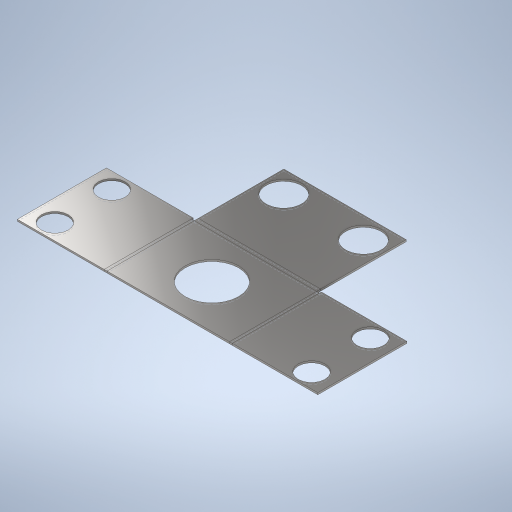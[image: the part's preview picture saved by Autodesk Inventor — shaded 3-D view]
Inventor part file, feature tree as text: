
AUTODESK INVENTOR PART (.ipt)
format: ipt  version: 2024 (Build 280153000, 153)  size: 375,296 bytes
history: native  units: mm
features: other x17, sketch x8, hole x4
ambient origin geometry x8: Origin, YZ Plane, XZ Plane, XY Plane, X Axis, Y Axis, Z Axis, Center Point
bodies: Volumenkörper1 (feature_tree)
feature tree (29):
  other  "Fläche1"
  other  "Lasche1"
  other  "Lasche2"
  other  "Lasche3"
  hole  "Bohrung1"  [1 undecoded]
  hole  "Bohrung2"  [1 undecoded]
  hole  "Bohrung3"  [1 undecoded]
  hole  "Bohrung4"  [1 undecoded]
  other  "Abwickeln1"
  other  "Abwickeln2"
  other  "Abwickeln3"
  sketch  "Skizze1"  dims[d0=25.0mm d1=35.0mm]
  other  "Grobblech1"
  sketch  "Skizze2"  dims[d2=0.5mm d3=0.5mm]
  other  "Grobblech2"
  other  "Biegung1"
  other  "Ecke1"
  sketch  "Skizze3"  dims[d4=0.25mm d5=1.0mm]
  other  "Grobblech3"
  other  "Biegung2"
  other  "Ecke2"
  sketch  "Skizze4"  dims[d6=0.5mm d7=25.0mm d8=11.34464mm d9=0.5mm]
  other  "Grobblech4"
  other  "Biegung3"
  other  "Ecke3"
  sketch  "Skizze5"  dims[d10=2.0mm]
  sketch  "Skizze7"  dims[d11=0.5mm]
  sketch  "Skizze8"  dims[d12=0.5mm]
  sketch  "Skizze9"  dims[d13=0.5mm d14=0.25mm d15=1.0mm d16=0.5mm d17=25.0mm d18=11.34464mm d19=0.5mm d20=2.0mm d21=0.5mm d22=0.5mm d23=0.5mm d24=0.25mm d25=1.0mm d26=0.5mm d27=25.0mm d28=90.0deg d29=0.5mm d30=2.0mm d31=0.5mm d32=0.5mm d33=16.0mm d34=6.0mm d35=7.5mm d36=6.0mm d37=4.0mm d38=2.0mm d39=90.0deg d40=0.5mm d41=20.594885mm d43=16.5mm d44=6.0mm d45=7.5mm d46=6.0mm d47=4.0mm d48=2.0mm d49=90.0deg d50=8.0mm d51=20.594885mm d52=15.0mm d53=6.0mm d54=4.0mm d55=2.0mm d56=90.0deg d57=8.0mm d58=20.594885mm d59=6.0mm d60=6.0mm d61=10.0mm d62=6.0mm d63=4.0mm d64=2.0mm d65=90.0deg d66=8.0mm d67=20.594885mm]
note: 4 required parameter values undecoded (feature->parameter linkage not recoverable at this tier; creation-order binding heuristic only, values carry confidence <= 0.55)
